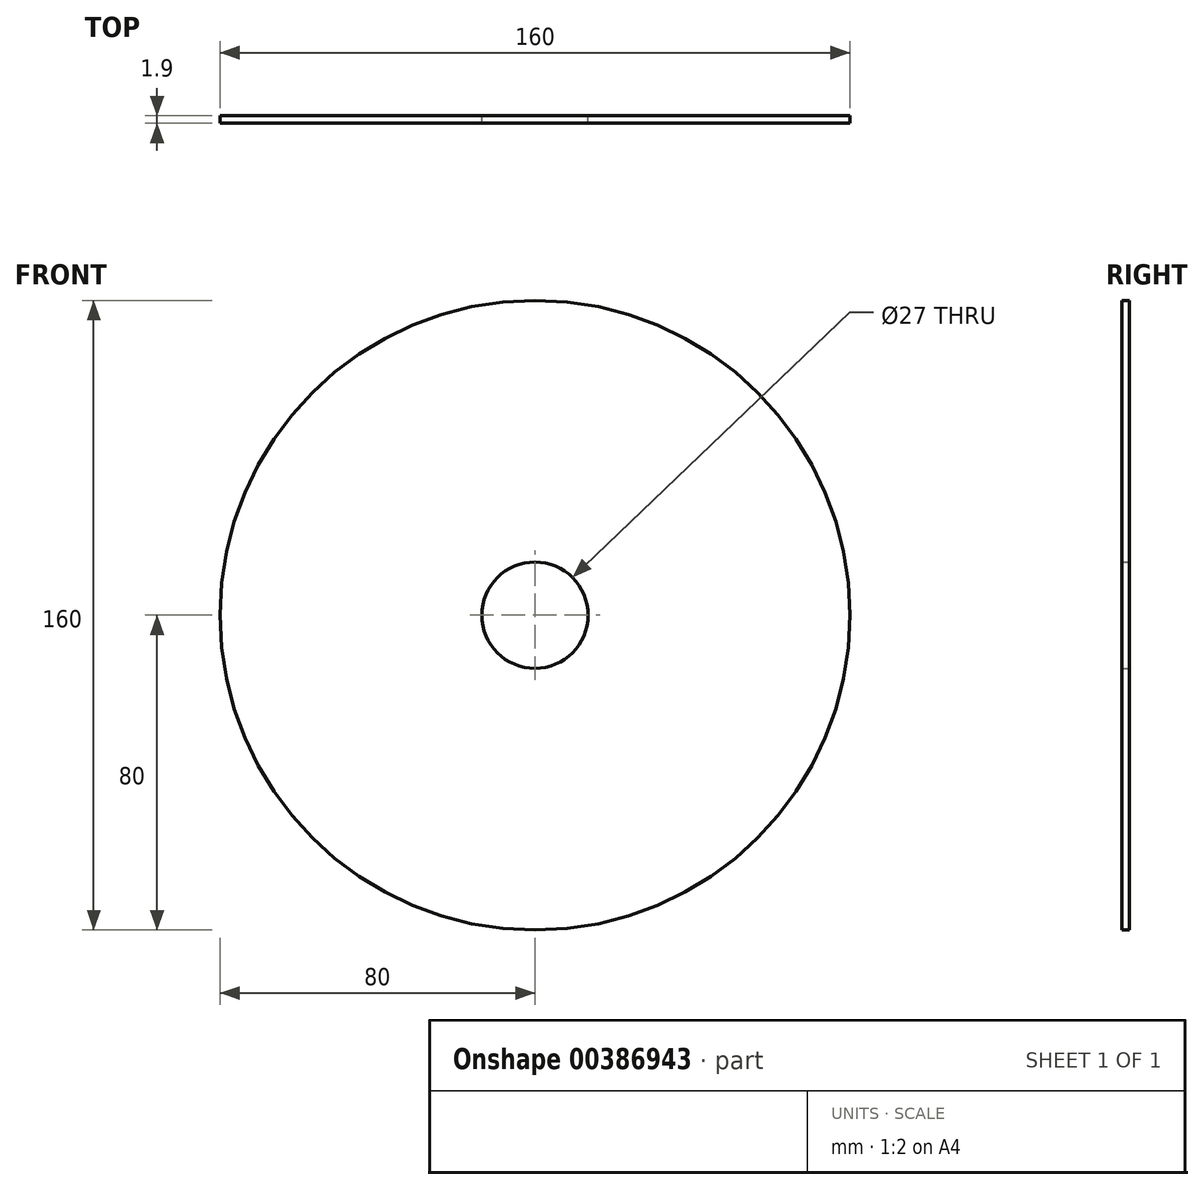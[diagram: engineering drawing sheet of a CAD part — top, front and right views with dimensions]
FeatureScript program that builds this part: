
annotation { "Feature Type Name" : "Feature", "Feature Type Description" : "" }
export const myFeature = defineFeature(function(context is Context, id is Id, definition is map)
    precondition{}
    {
        {
            var Q0;
            Q0=qCreatedBy(makeId("Front.planeOp"),FACE);
            var sketch = newSketch(context, id + "F0", { "sketchPlane" : qUnion([Q0])});
            skCircle(sketch, "E0", {"center": v(0, 0) * mm, "radius": 80 * mm});
            skCircle(sketch, "E1", {"center": v(0, 0) * mm, "radius": 13.5 * mm});
            skSolve(sketch);
        }
        {
            var Q0;
            Q0=qSketchRegion(id+"F0",true);
            extrude(context, id + "F1", {"entities" : qUnion([Q0]), "depth" : 1.9 * mm});
        }
    });
